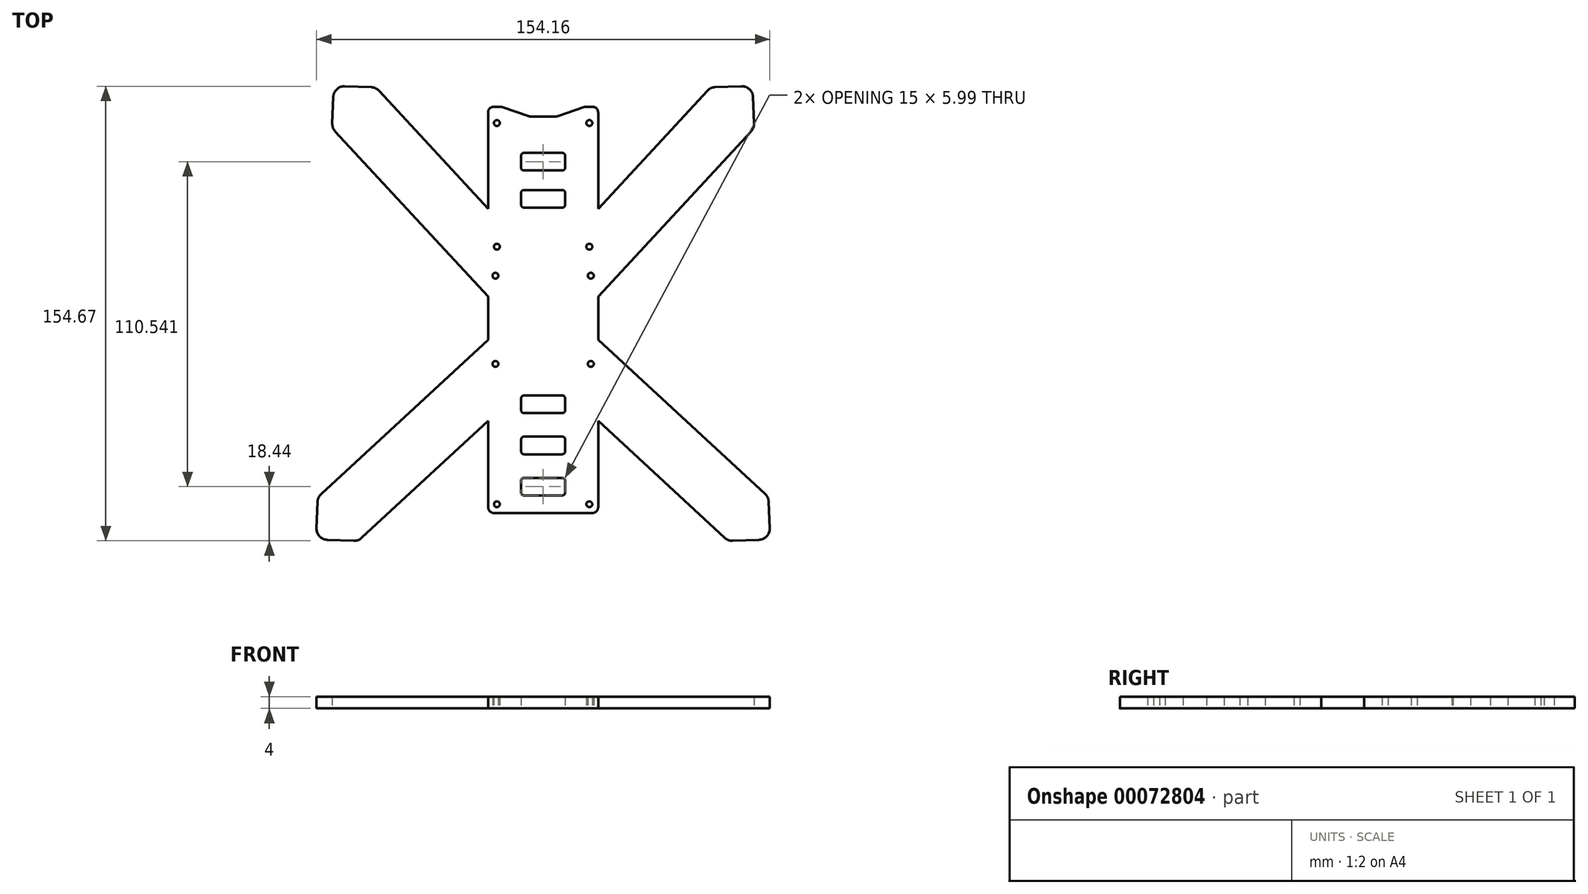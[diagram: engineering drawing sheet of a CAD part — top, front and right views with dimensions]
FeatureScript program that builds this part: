
annotation { "Feature Type Name" : "Feature", "Feature Type Description" : "" }
export const myFeature = defineFeature(function(context is Context, id is Id, definition is map)
    precondition{}
    {
        {
            var Q0;
            Q0=qCreatedBy(makeId("Top.planeOp"),FACE);
            var sketch = newSketch(context, id + "F0", { "sketchPlane" : qUnion([Q0])});
            skLineSegment(sketch, "E0", {"start": v(-18.72, 62.62) * mm, "end": v(-18.72, 29.94) * mm});
            skLineSegment(sketch, "E1", {"start": v(-16.72, 64.62) * mm, "end": v(-14.73, 64.62) * mm});
            skLineSegment(sketch, "E2", {"start": v(-14.08, 64.51) * mm, "end": v(-4.88, 61.39) * mm});
            skLineSegment(sketch, "E3", {"start": v(-4.23, 61.28) * mm, "end": v(0, 61.28) * mm});
            skLineSegment(sketch, "E4.MirrorCS", {"start": v(18.72, 64.62) * mm, "end": v(18.7, 64.62) * mm});
            skArc(sketch, "E5.filletArc", {"start": v(-16.72, 64.62) * mm, "mid": v(-18.13, 64.03) * mm, "end": v(-18.72, 62.62) * mm});
            skArc(sketch, "E6.filletArc", {"start": v(-14.08, 64.51) * mm, "mid": v(-14.4, 64.6) * mm, "end": v(-14.73, 64.62) * mm});
            skArc(sketch, "E7.filletArc", {"start": v(-4.88, 61.39) * mm, "mid": v(-4.56, 61.3) * mm, "end": v(-4.23, 61.28) * mm});
            skPoint(sketch, "E8.visualSharp", {"position": v(18.7, -73.5) * mm});
            skPoint(sketch, "E9.visualSharp", {"position": v(-18.72, -73.63) * mm});
            skArc(sketch, "E9.filletArc", {"start": v(-18.72, -71.63) * mm, "mid": v(-18.13, -73.04) * mm, "end": v(-16.72, -73.63) * mm});
            skLineSegment(sketch, "E10", {"start": v(-16.72, -73.63) * mm, "end": v(0, -73.63) * mm});
            skLineSegment(sketch, "E11.MirrorCS", {"start": v(16.72, -73.63) * mm, "end": v(0, -73.63) * mm});
            skArc(sketch, "E12.MirrorCS", {"start": v(18.72, -71.63) * mm, "mid": v(18.13, -73.04) * mm, "end": v(16.72, -73.63) * mm});
            skLineSegment(sketch, "E13.MirrorCS", {"start": v(18.72, 62.62) * mm, "end": v(18.72, 29.94) * mm});
            skArc(sketch, "E14.MirrorCS", {"start": v(16.72, 64.62) * mm, "mid": v(18.13, 64.03) * mm, "end": v(18.72, 62.62) * mm});
            skLineSegment(sketch, "E15.MirrorCS", {"start": v(16.72, 64.62) * mm, "end": v(14.73, 64.62) * mm});
            skArc(sketch, "E16.MirrorCS", {"start": v(14.08, 64.51) * mm, "mid": v(14.4, 64.6) * mm, "end": v(14.73, 64.62) * mm});
            skLineSegment(sketch, "E17.MirrorCS", {"start": v(14.08, 64.51) * mm, "end": v(4.88, 61.39) * mm});
            skArc(sketch, "E18.MirrorCS", {"start": v(4.88, 61.39) * mm, "mid": v(4.56, 61.3) * mm, "end": v(4.23, 61.28) * mm});
            skLineSegment(sketch, "E19.MirrorCS", {"start": v(4.23, 61.28) * mm, "end": v(0, 61.28) * mm});
            skLineSegment(sketch, "E20", {"start": v(0, -67.63) * mm, "end": v(-6.5, -67.63) * mm});
            skLineSegment(sketch, "E21", {"start": v(-7.5, -66.63) * mm, "end": v(-7.5, -62.63) * mm});
            skLineSegment(sketch, "E22", {"start": v(-6.5, -61.63) * mm, "end": v(0, -61.63) * mm});
            skLineSegment(sketch, "E23", {"start": v(0, -39.63) * mm, "end": v(6.5, -39.63) * mm});
            skLineSegment(sketch, "E24", {"start": v(7.5, -38.63) * mm, "end": v(7.5, -34.63) * mm});
            skLineSegment(sketch, "E25", {"start": v(6.5, -33.63) * mm, "end": v(0, -33.63) * mm});
            skLineSegment(sketch, "E26", {"start": v(0, 36.28) * mm, "end": v(6.5, 36.28) * mm});
            skLineSegment(sketch, "E27", {"start": v(7.5, 35.28) * mm, "end": v(7.5, 31.28) * mm});
            skLineSegment(sketch, "E28", {"start": v(6.5, 30.28) * mm, "end": v(0, 30.28) * mm});
            skLineSegment(sketch, "E29.MirrorCS", {"start": v(0, 36.28) * mm, "end": v(-6.5, 36.28) * mm});
            skLineSegment(sketch, "E30.MirrorCS", {"start": v(-7.5, 35.28) * mm, "end": v(-7.5, 31.28) * mm});
            skLineSegment(sketch, "E31.MirrorCS", {"start": v(-6.5, 30.28) * mm, "end": v(0, 30.28) * mm});
            skArc(sketch, "E32.filletArc", {"start": v(-6.5, 36.28) * mm, "mid": v(-7.2, 35.99) * mm, "end": v(-7.5, 35.28) * mm});
            skArc(sketch, "E33.filletArc", {"start": v(-7.5, 31.28) * mm, "mid": v(-7.2, 30.57) * mm, "end": v(-6.5, 30.28) * mm});
            skArc(sketch, "E34.filletArc", {"start": v(6.5, 30.28) * mm, "mid": v(7.2, 30.57) * mm, "end": v(7.5, 31.28) * mm});
            skArc(sketch, "E35.filletArc", {"start": v(7.5, 35.28) * mm, "mid": v(7.2, 35.99) * mm, "end": v(6.5, 36.28) * mm});
            skLineSegment(sketch, "E36.MirrorCS", {"start": v(6.5, -61.63) * mm, "end": v(0, -61.63) * mm});
            skLineSegment(sketch, "E37.MirrorCS", {"start": v(7.5, -66.63) * mm, "end": v(7.5, -62.63) * mm});
            skLineSegment(sketch, "E38.MirrorCS", {"start": v(0, -67.63) * mm, "end": v(6.5, -67.63) * mm});
            skLineSegment(sketch, "E39.MirrorCS", {"start": v(-6.5, -33.63) * mm, "end": v(0, -33.63) * mm});
            skLineSegment(sketch, "E40.MirrorCS", {"start": v(-7.5, -38.63) * mm, "end": v(-7.5, -34.63) * mm});
            skLineSegment(sketch, "E41.MirrorCS", {"start": v(0, -39.63) * mm, "end": v(-6.5, -39.63) * mm});
            skLineSegment(sketch, "E42", {"start": v(0, -53.62) * mm, "end": v(6.5, -53.62) * mm});
            skLineSegment(sketch, "E43", {"start": v(0, -47.62) * mm, "end": v(6.5, -47.62) * mm});
            skLineSegment(sketch, "E44", {"start": v(7.5, -48.62) * mm, "end": v(7.5, -52.62) * mm});
            skLineSegment(sketch, "E45.MirrorCS", {"start": v(0, -47.62) * mm, "end": v(-6.5, -47.62) * mm});
            skLineSegment(sketch, "E46.MirrorCS", {"start": v(-7.5, -48.62) * mm, "end": v(-7.5, -52.62) * mm});
            skLineSegment(sketch, "E47.MirrorCS", {"start": v(0, -53.62) * mm, "end": v(-6.5, -53.62) * mm});
            skArc(sketch, "E48.filletArc", {"start": v(-6.5, -33.63) * mm, "mid": v(-7.2, -33.93) * mm, "end": v(-7.5, -34.63) * mm});
            skArc(sketch, "E49.filletArc", {"start": v(-7.5, -38.63) * mm, "mid": v(-7.2, -39.33) * mm, "end": v(-6.5, -39.63) * mm});
            skArc(sketch, "E50.filletArc", {"start": v(6.5, -39.63) * mm, "mid": v(7.2, -39.33) * mm, "end": v(7.5, -38.63) * mm});
            skArc(sketch, "E51.filletArc", {"start": v(7.5, -34.63) * mm, "mid": v(7.2, -33.93) * mm, "end": v(6.5, -33.63) * mm});
            skArc(sketch, "E52.filletArc", {"start": v(7.5, -48.62) * mm, "mid": v(7.2, -47.92) * mm, "end": v(6.5, -47.62) * mm});
            skArc(sketch, "E53.filletArc", {"start": v(-6.5, -47.62) * mm, "mid": v(-7.2, -47.92) * mm, "end": v(-7.5, -48.62) * mm});
            skArc(sketch, "E54.filletArc", {"start": v(-7.5, -52.62) * mm, "mid": v(-7.2, -53.33) * mm, "end": v(-6.5, -53.62) * mm});
            skArc(sketch, "E55.filletArc", {"start": v(6.5, -53.62) * mm, "mid": v(7.2, -53.33) * mm, "end": v(7.5, -52.62) * mm});
            skArc(sketch, "E56.filletArc", {"start": v(-6.5, -61.63) * mm, "mid": v(-7.2, -61.93) * mm, "end": v(-7.5, -62.63) * mm});
            skArc(sketch, "E57.filletArc", {"start": v(-7.5, -66.63) * mm, "mid": v(-7.2, -67.33) * mm, "end": v(-6.5, -67.63) * mm});
            skArc(sketch, "E58.filletArc", {"start": v(6.5, -67.63) * mm, "mid": v(7.2, -67.33) * mm, "end": v(7.5, -66.63) * mm});
            skArc(sketch, "E59.filletArc", {"start": v(7.5, -62.63) * mm, "mid": v(7.2, -61.93) * mm, "end": v(6.5, -61.63) * mm});
            skCircle(sketch, "E60", {"center": v(-15.72, -70.63) * mm, "radius": 1 * mm});
            skCircle(sketch, "E61.MirrorC", {"center": v(15.72, -70.63) * mm, "radius": 1 * mm});
            skCircle(sketch, "E62", {"center": v(-15.72, 59.06) * mm, "radius": 1 * mm});
            skLineSegment(sketch, "E63", {"start": v(15.72, 59.06) * mm, "end": v(15.72, 59.06) * mm});
            skCircle(sketch, "E64.MirrorC", {"center": v(-15.72, 17) * mm, "radius": 1 * mm});
            skCircle(sketch, "E65", {"center": v(16.22, 7.12) * mm, "radius": 1 * mm});
            skCircle(sketch, "E66", {"center": v(16.22, -22.88) * mm, "radius": 1 * mm});
            skCircle(sketch, "E67.MirrorC", {"center": v(15.72, 17) * mm, "radius": 1 * mm});
            skCircle(sketch, "E68.MirrorC", {"center": v(-16.22, 7.12) * mm, "radius": 1 * mm});
            skCircle(sketch, "E69.MirrorC", {"center": v(-16.22, -22.88) * mm, "radius": 1 * mm});
            skPoint(sketch, "E70.start.orphan", {"position": v(0, -7.88) * mm});
            skLineSegment(sketch, "E71", {"start": v(-6.5, 42.91) * mm, "end": v(6.5, 42.91) * mm});
            skLineSegment(sketch, "E72", {"start": v(-7.5, 43.91) * mm, "end": v(-7.5, 47.9) * mm});
            skLineSegment(sketch, "E73", {"start": v(-6.5, 48.9) * mm, "end": v(6.5, 48.9) * mm});
            skLineSegment(sketch, "E74", {"start": v(7.5, 43.91) * mm, "end": v(7.5, 47.9) * mm});
            skArc(sketch, "E75.filletArc", {"start": v(-6.5, 48.9) * mm, "mid": v(-7.2, 48.62) * mm, "end": v(-7.5, 47.9) * mm});
            skArc(sketch, "E76.filletArc", {"start": v(-7.5, 43.91) * mm, "mid": v(-7.2, 43.2) * mm, "end": v(-6.5, 42.91) * mm});
            skArc(sketch, "E77.filletArc", {"start": v(6.5, 42.91) * mm, "mid": v(7.2, 43.2) * mm, "end": v(7.5, 43.91) * mm});
            skArc(sketch, "E78.filletArc", {"start": v(7.5, 47.9) * mm, "mid": v(7.2, 48.62) * mm, "end": v(6.5, 48.9) * mm});
            skCircle(sketch, "E79.MirrorC", {"center": v(15.72, 59.06) * mm, "radius": 1 * mm});
            skLineSegment(sketch, "E80", {"start": v(-18.72, -14.63) * mm, "end": v(-75.5, -67.14) * mm});
            skLineSegment(sketch, "E81", {"start": v(-18.72, 0) * mm, "end": v(-70.71, 56.23) * mm});
            skLineSegment(sketch, "E82.MirrorCS", {"start": v(18.72, 0) * mm, "end": v(71.78, 57.39) * mm});
            skLineSegment(sketch, "E83.MirrorCS", {"start": v(18.72, -14.63) * mm, "end": v(76.67, -68.21) * mm});
            skLineSegment(sketch, "E84", {"start": v(-55.8, 70.03) * mm, "end": v(-18.72, 29.94) * mm});
            skLineSegment(sketch, "E85", {"start": v(-61.71, -82.06) * mm, "end": v(-18.72, -42.3) * mm});
            skLineSegment(sketch, "E86.MirrorCS", {"start": v(62.87, -83.13) * mm, "end": v(18.72, -42.3) * mm});
            skLineSegment(sketch, "E87.MirrorCS", {"start": v(56.87, 71.18) * mm, "end": v(18.72, 29.94) * mm});
            skLineSegment(sketch, "E88.trimOffspring", {"start": v(-18.72, 0) * mm, "end": v(-18.72, -14.63) * mm});
            skLineSegment(sketch, "E89.trimOffspring", {"start": v(18.72, 0) * mm, "end": v(18.72, -14.63) * mm});
            skLineSegment(sketch, "E90.trimOffspring", {"start": v(18.72, -42.3) * mm, "end": v(18.72, -71.63) * mm});
            skLineSegment(sketch, "E91.trimOffspring", {"start": v(-18.72, -42.3) * mm, "end": v(-18.72, -71.63) * mm});
            skLineSegment(sketch, "E92", {"start": v(-71.37, 67.94) * mm, "end": v(-71.72, 58.97) * mm});
            skLineSegment(sketch, "E93", {"start": v(-67.42, 71.6) * mm, "end": v(-58.44, 71.25) * mm});
            skLineSegment(sketch, "E94", {"start": v(-76.73, -69.8) * mm, "end": v(-77.08, -78.76) * mm});
            skLineSegment(sketch, "E95", {"start": v(-73.42, -82.72) * mm, "end": v(-64.45, -83.07) * mm});
            skPoint(sketch, "E96.visualSharp", {"position": v(-77.23, -82.57) * mm});
            skArc(sketch, "E96.filletArc", {"start": v(-77.08, -78.76) * mm, "mid": v(-76.07, -81.5) * mm, "end": v(-73.42, -82.72) * mm});
            skPoint(sketch, "E97.visualSharp", {"position": v(-71.22, 71.75) * mm});
            skArc(sketch, "E97.filletArc", {"start": v(-67.42, 71.6) * mm, "mid": v(-70.15, 70.59) * mm, "end": v(-71.37, 67.94) * mm});
            skPoint(sketch, "E98.visualSharp", {"position": v(-71.78, 57.39) * mm});
            skArc(sketch, "E98.filletArc", {"start": v(-71.72, 58.97) * mm, "mid": v(-71.5, 57.5) * mm, "end": v(-70.71, 56.23) * mm});
            skPoint(sketch, "E99.visualSharp", {"position": v(-56.87, 71.18) * mm});
            skArc(sketch, "E99.filletArc", {"start": v(-55.8, 70.03) * mm, "mid": v(-57, 70.9) * mm, "end": v(-58.44, 71.25) * mm});
            skPoint(sketch, "E100.visualSharp", {"position": v(-76.67, -68.21) * mm});
            skArc(sketch, "E100.filletArc", {"start": v(-75.5, -67.14) * mm, "mid": v(-76.38, -68.35) * mm, "end": v(-76.73, -69.8) * mm});
            skPoint(sketch, "E101.visualSharp", {"position": v(-62.87, -83.13) * mm});
            skArc(sketch, "E101.filletArc", {"start": v(-64.45, -83.07) * mm, "mid": v(-62.98, -82.84) * mm, "end": v(-61.71, -82.06) * mm});
            skPoint(sketch, "E102.MirrorCS.end.orphan", {"position": v(62.87, -83.13) * mm});
            skPoint(sketch, "E102.MirrorCS.start.orphan", {"position": v(76.67, -68.21) * mm});
            skPoint(sketch, "E103.MirrorCS.end.orphan", {"position": v(56.87, 71.18) * mm});
            skPoint(sketch, "E103.MirrorCS.start.orphan", {"position": v(71.78, 57.39) * mm});
            skArc(sketch, "E104.MirrorCS", {"start": v(64.45, -83.07) * mm, "mid": v(62.98, -82.84) * mm, "end": v(61.71, -82.06) * mm});
            skLineSegment(sketch, "E105.MirrorCS", {"start": v(73.42, -82.72) * mm, "end": v(64.45, -83.07) * mm});
            skArc(sketch, "E106.MirrorCS", {"start": v(77.08, -78.76) * mm, "mid": v(76.07, -81.5) * mm, "end": v(73.42, -82.72) * mm});
            skLineSegment(sketch, "E107.MirrorCS", {"start": v(76.73, -69.8) * mm, "end": v(77.08, -78.76) * mm});
            skArc(sketch, "E108.MirrorCS", {"start": v(75.5, -67.14) * mm, "mid": v(76.38, -68.35) * mm, "end": v(76.73, -69.8) * mm});
            skLineSegment(sketch, "E109.MirrorCS", {"start": v(71.37, 67.94) * mm, "end": v(71.72, 58.97) * mm});
            skLineSegment(sketch, "E110.MirrorCS", {"start": v(67.42, 71.6) * mm, "end": v(58.44, 71.25) * mm});
            skArc(sketch, "E111.MirrorCS", {"start": v(71.72, 58.97) * mm, "mid": v(71.5, 57.5) * mm, "end": v(70.71, 56.23) * mm});
            skArc(sketch, "E112.MirrorCS", {"start": v(67.42, 71.6) * mm, "mid": v(70.15, 70.59) * mm, "end": v(71.37, 67.94) * mm});
            skArc(sketch, "E113.MirrorCS", {"start": v(55.8, 70.03) * mm, "mid": v(57, 70.9) * mm, "end": v(58.44, 71.25) * mm});
            skSolve(sketch);
        }
        {
            var Q0;
            Q0=makeQuery(id+"F0.imprint","IMPRINT",FACE,{"disambiguationData":[TD([[makeQuery(id+"F0.imprint","IMPRINT",EDGE,{"derivedFrom":sQuery(id+"F0.wireOp",EDGE,"E0")}),1.0]])]});
            extrude(context, id + "F1", {"entities" : qUnion([Q0]), "depth" : 4 * mm});
        }
    });
